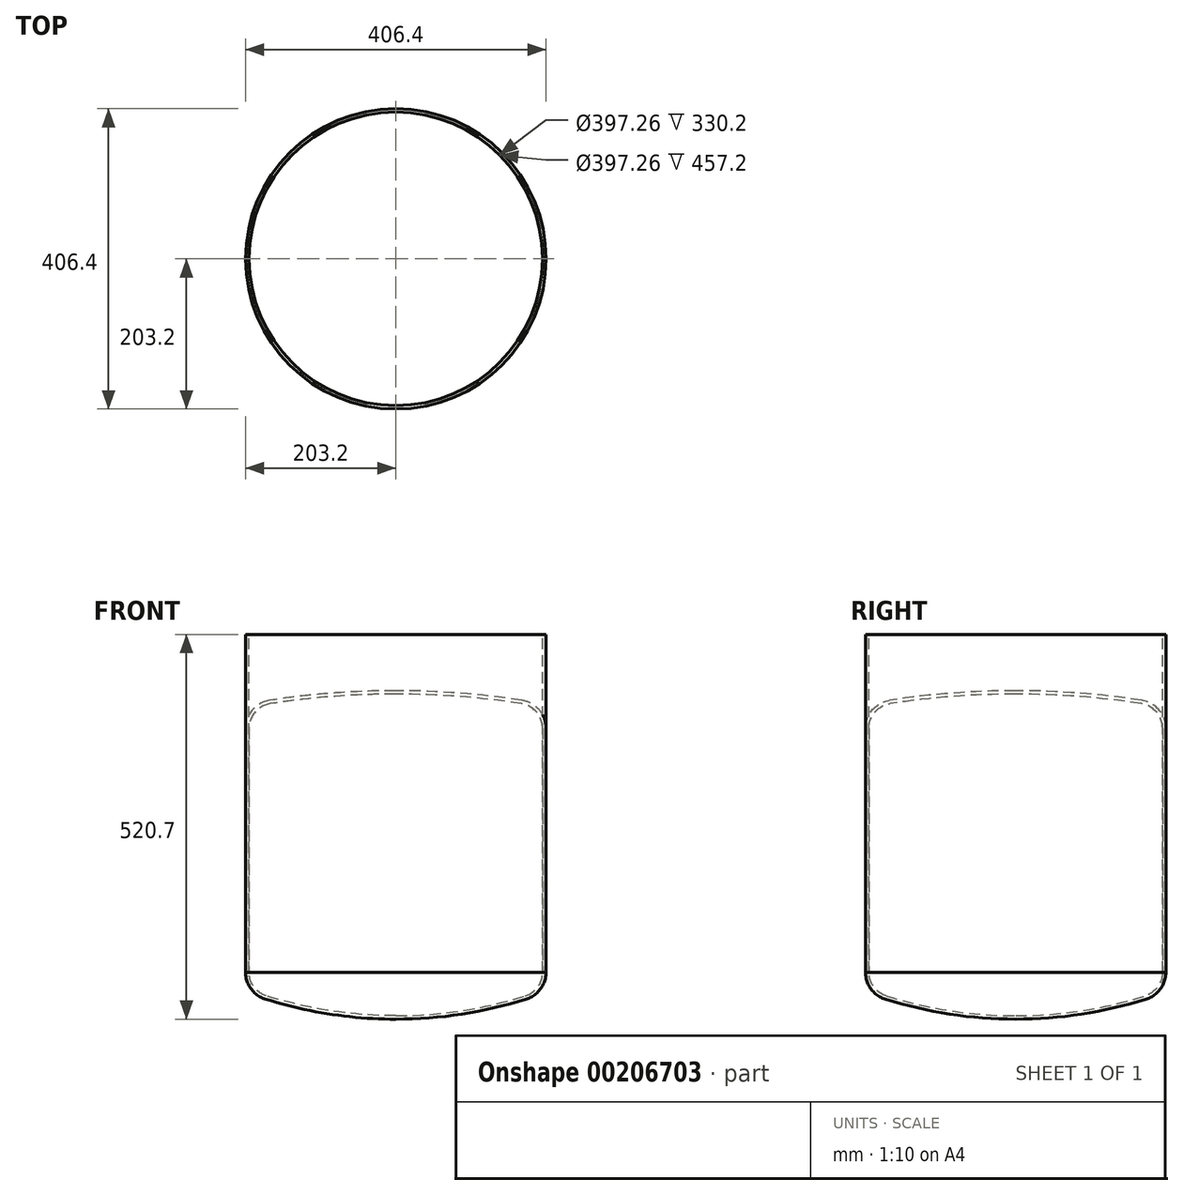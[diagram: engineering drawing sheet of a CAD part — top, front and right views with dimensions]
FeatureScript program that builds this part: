
annotation { "Feature Type Name" : "Feature", "Feature Type Description" : "" }
export const myFeature = defineFeature(function(context is Context, id is Id, definition is map)
    precondition{}
    {
        {
            var Q0;
            Q0=qCreatedBy(makeId("Front.planeOp"),FACE);
            var sketch = newSketch(context, id + "F0", { "sketchPlane" : qUnion([Q0])});
            skLineSegment(sketch, "E0.bottom", {"start": v(-198.63, 457.2) * mm, "end": v(-203.2, 457.2) * mm});
            skLineSegment(sketch, "E0.right", {"start": v(-203.2, 457.2) * mm, "end": v(-203.2, 0) * mm});
            skPoint(sketch, "E0.middle", {"position": v(0, 0) * mm});
            skArc(sketch, "E1", {"start": v(-176.55, -36.34) * mm, "mid": v(-89.31, -56.67) * mm, "end": v(0, -63.5) * mm});
            skPoint(sketch, "E2.visualSharp", {"position": v(-203.2, -27.23) * mm});
            skArc(sketch, "E2.filletArc", {"start": v(-203.2, 0) * mm, "mid": v(-195.82, -22.53) * mm, "end": v(-176.55, -36.34) * mm});
            skLineSegment(sketch, "E3", {"start": v(-203.2, 0) * mm, "end": v(0, 0) * mm, "construction": true});
            skPoint(sketch, "E4", {"position": v(0, -63.5) * mm});
            skLineSegment(sketch, "E5", {"start": v(0, 457.2) * mm, "end": v(0, -58.93) * mm, "construction": true});
            skArc(sketch, "E6.0", {"start": v(-175.18, -31.98) * mm, "mid": v(-88.62, -52.15) * mm, "end": v(0, -58.93) * mm});
            skArc(sketch, "E6.1", {"start": v(-198.63, 0) * mm, "mid": v(-192.14, -19.83) * mm, "end": v(-175.18, -31.98) * mm});
            skLineSegment(sketch, "E6.2", {"start": v(-198.63, 457.2) * mm, "end": v(-198.63, 0) * mm});
            skLineSegment(sketch, "E7", {"start": v(0, -58.93) * mm, "end": v(0, -63.5) * mm});
            skSolve(sketch);
        }
        {
            var Q0;
            Q0 = qSketchRegion(id + "F0", true);
            var Q1;
            Q1=sQuery(id+"F0.wireOp",EDGE,"E5");
            revolve(context, id + "F1", {"entities" : qUnion([Q0]), "axis" : qUnion([Q1]), "revolveType" : RevolveType.FULL});
        }
        {
            var Q0;
            Q0=qCreatedBy(makeId("Front.planeOp"),FACE);
            var sketch = newSketch(context, id + "F2", { "sketchPlane" : qUnion([Q0])});
            skLineSegment(sketch, "E8", {"start": v(-203.2, 0) * mm, "end": v(-198.63, 0) * mm});
            skLineSegment(sketch, "E9", {"start": v(-203.2, 330.2) * mm, "end": v(-203.2, 0) * mm});
            skLineSegment(sketch, "E10", {"start": v(0, 4.57) * mm, "end": v(0, 376.43) * mm, "construction": true});
            skArc(sketch, "E11", {"start": v(0, 381) * mm, "mid": v(-85.72, 377.7) * mm, "end": v(-170.93, 367.85) * mm});
            skPoint(sketch, "E12.visualSharp", {"position": v(-203.2, 362.37) * mm});
            skArc(sketch, "E12.filletArc", {"start": v(-170.93, 367.85) * mm, "mid": v(-194.03, 355) * mm, "end": v(-203.2, 330.2) * mm});
            skLineSegment(sketch, "E13.1", {"start": v(-198.63, 330.2) * mm, "end": v(-198.63, 0) * mm});
            skArc(sketch, "E13.2", {"start": v(-170.23, 363.33) * mm, "mid": v(-190.56, 352.02) * mm, "end": v(-198.63, 330.2) * mm});
            skArc(sketch, "E13.3", {"start": v(0, 376.43) * mm, "mid": v(-85.37, 373.15) * mm, "end": v(-170.23, 363.33) * mm});
            skLineSegment(sketch, "E14", {"start": v(0, 381) * mm, "end": v(0, 376.43) * mm});
            skSolve(sketch);
        }
        {
            var Q0;
            Q0 = qSketchRegion(id + "F2", true);
            var Q1;
            Q1=sQuery(id+"F2.wireOp",EDGE,"E10");
            revolve(context, id + "F3", {"entities" : qUnion([Q0]), "axis" : qUnion([Q1]), "revolveType" : RevolveType.FULL});
        }
    });
